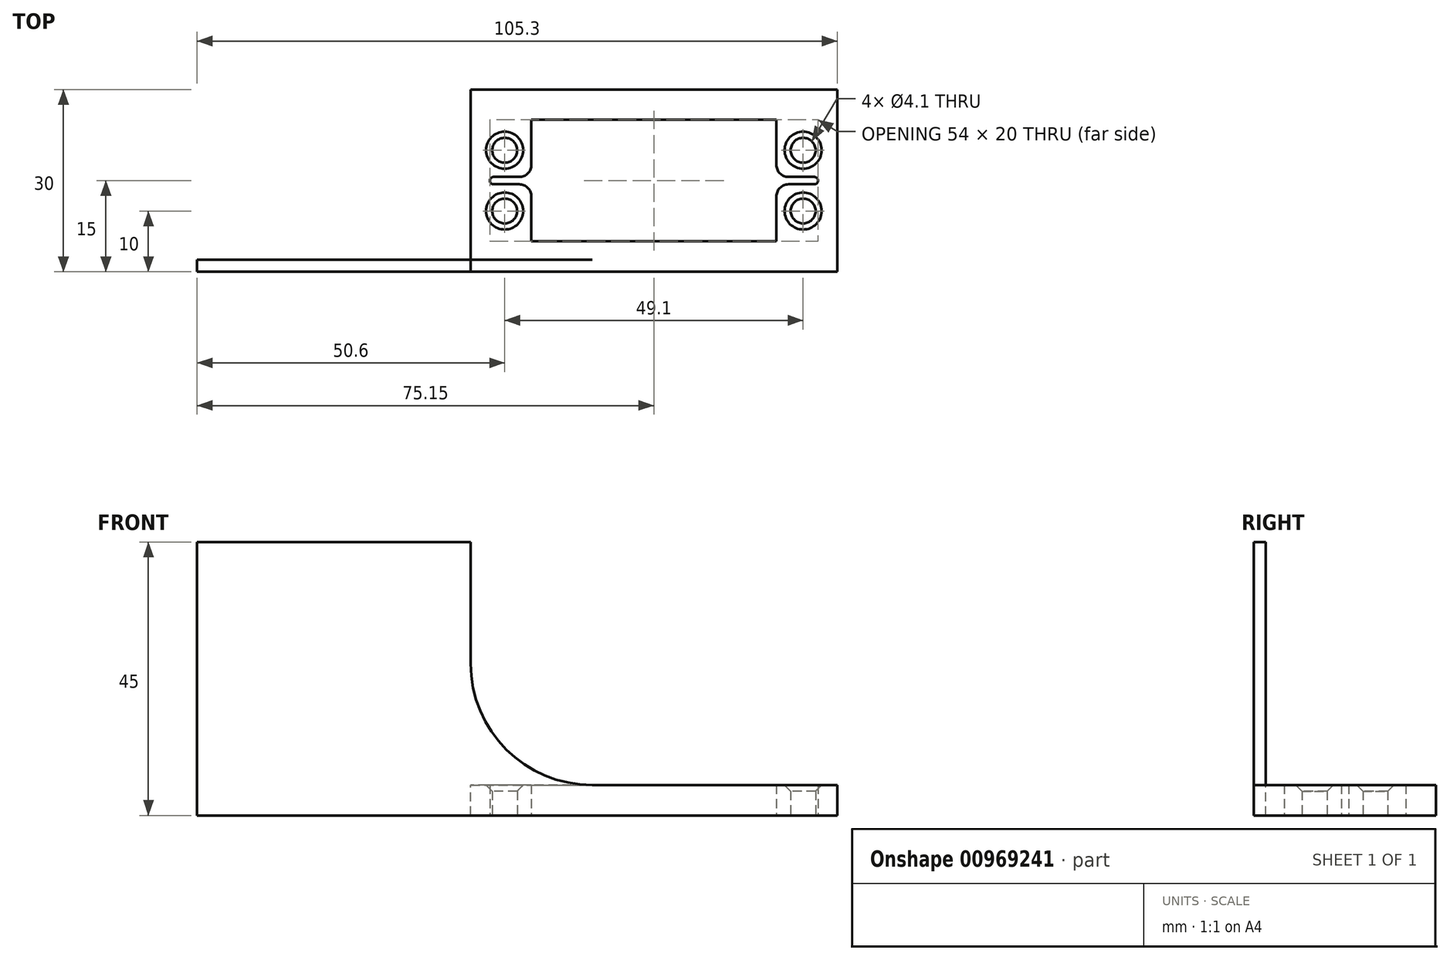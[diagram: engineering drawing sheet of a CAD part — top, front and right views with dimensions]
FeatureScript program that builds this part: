
annotation { "Feature Type Name" : "Feature", "Feature Type Description" : "" }
export const myFeature = defineFeature(function(context is Context, id is Id, definition is map)
    precondition{}
    {
        {
            var Q0;
            Q0=qCreatedBy(makeId("Top.planeOp"),FACE);
            var sketch = newSketch(context, id + "F0", { "sketchPlane" : qUnion([Q0])});
            skLineSegment(sketch, "E0.bottom", {"start": v(30.15, -15) * mm, "end": v(-30.15, -15) * mm});
            skLineSegment(sketch, "E0.top", {"start": v(30.15, 15) * mm, "end": v(-30.15, 15) * mm});
            skLineSegment(sketch, "E0.left", {"start": v(30.15, -15) * mm, "end": v(30.15, 15) * mm});
            skLineSegment(sketch, "E0.right", {"start": v(-30.15, -15) * mm, "end": v(-30.15, 15) * mm});
            skPoint(sketch, "E0.middle", {"position": v(0, 0) * mm});
            skLineSegment(sketch, "E1", {"start": v(0, 10) * mm, "end": v(20.15, 10) * mm});
            skLineSegment(sketch, "E2", {"start": v(20.15, 10) * mm, "end": v(20.15, 2.6) * mm});
            skLineSegment(sketch, "E3", {"start": v(22.15, 0.6) * mm, "end": v(26.4, 0.6) * mm});
            skLineSegment(sketch, "E4", {"start": v(27, 0) * mm, "end": v(27, 0) * mm});
            skPoint(sketch, "E5.visualSharp", {"position": v(27, 0.6) * mm});
            skArc(sketch, "E5.filletArc", {"start": v(27, 0) * mm, "mid": v(26.82, 0.42) * mm, "end": v(26.4, 0.6) * mm});
            skPoint(sketch, "E6.visualSharp", {"position": v(20.15, 0.6) * mm});
            skArc(sketch, "E6.filletArc", {"start": v(20.15, 2.6) * mm, "mid": v(20.74, 1.19) * mm, "end": v(22.15, 0.6) * mm});
            skLineSegment(sketch, "E7.MirrorCS", {"start": v(0, -10) * mm, "end": v(20.15, -10) * mm});
            skLineSegment(sketch, "E8.MirrorCS", {"start": v(20.15, -10) * mm, "end": v(20.15, -2.6) * mm});
            skArc(sketch, "E9.MirrorCS", {"start": v(20.15, -2.6) * mm, "mid": v(20.74, -1.19) * mm, "end": v(22.15, -0.6) * mm});
            skArc(sketch, "E10.MirrorCS", {"start": v(27, 0) * mm, "mid": v(26.82, -0.42) * mm, "end": v(26.4, -0.6) * mm});
            skLineSegment(sketch, "E11.MirrorCS", {"start": v(22.15, -0.6) * mm, "end": v(26.4, -0.6) * mm});
            skLineSegment(sketch, "E12.MirrorCS", {"start": v(0, 10) * mm, "end": v(-20.15, 10) * mm});
            skLineSegment(sketch, "E13.MirrorCS", {"start": v(-20.15, 10) * mm, "end": v(-20.15, 2.6) * mm});
            skArc(sketch, "E14.MirrorCS", {"start": v(-20.15, 2.6) * mm, "mid": v(-20.74, 1.19) * mm, "end": v(-22.15, 0.6) * mm});
            skLineSegment(sketch, "E15.MirrorCS", {"start": v(-22.15, 0.6) * mm, "end": v(-26.4, 0.6) * mm});
            skArc(sketch, "E16.MirrorCS", {"start": v(-27, 0) * mm, "mid": v(-26.82, -0.42) * mm, "end": v(-26.4, -0.6) * mm});
            skLineSegment(sketch, "E17.MirrorCS", {"start": v(-22.15, -0.6) * mm, "end": v(-26.4, -0.6) * mm});
            skArc(sketch, "E18.MirrorCS", {"start": v(-20.15, -2.6) * mm, "mid": v(-20.74, -1.19) * mm, "end": v(-22.15, -0.6) * mm});
            skLineSegment(sketch, "E19.MirrorCS", {"start": v(-20.15, -10) * mm, "end": v(-20.15, -2.6) * mm});
            skLineSegment(sketch, "E20.MirrorCS", {"start": v(0, -10) * mm, "end": v(-20.15, -10) * mm});
            skArc(sketch, "E21.MirrorCS", {"start": v(-27, 0) * mm, "mid": v(-26.82, 0.42) * mm, "end": v(-26.4, 0.6) * mm});
            skCircle(sketch, "E22", {"center": v(24.55, 5) * mm, "radius": 2.05 * mm});
            skCircle(sketch, "E23.MirrorC", {"center": v(-24.55, 5) * mm, "radius": 2.05 * mm});
            skCircle(sketch, "E24.MirrorC", {"center": v(-24.55, -5) * mm, "radius": 2.05 * mm});
            skCircle(sketch, "E25.MirrorC", {"center": v(24.55, -5) * mm, "radius": 2.05 * mm});
            skSolve(sketch);
        }
        {
            var Q0;
            Q0 = qSketchRegion(id + "F0", true);
            extrude(context, id + "F1", {"entities" : qUnion([Q0]), "depth" : 5 * mm, "offsetDistance" : 25 * mm});
        }
        {
            var Q0;
            Q0=makeQuery(id+"F1.opExtrude","SWEPT_FACE",FACE,{"disambiguationData":[OSD([sQuery(id+"F0.wireOp",EDGE,"E0.bottom")])]});
            var sketch = newSketch(context, id + "F2", { "sketchPlane" : qUnion([Q0])});
            skLineSegment(sketch, "E26", {"start": v(-10.03, 0) * mm, "end": v(-75.15, 0) * mm});
            skLineSegment(sketch, "E27", {"start": v(-75.15, 0) * mm, "end": v(-75.15, 45) * mm});
            skLineSegment(sketch, "E28", {"start": v(-75.15, 45) * mm, "end": v(-30.15, 45) * mm});
            skLineSegment(sketch, "E29", {"start": v(-30.15, 45) * mm, "end": v(-30.15, 25) * mm});
            skLineSegment(sketch, "E30", {"start": v(-10.03, 0) * mm, "end": v(-10.03, 5) * mm});
            skLineSegment(sketch, "E31", {"start": v(-10.03, 5) * mm, "end": v(-10.15, 5) * mm});
            skPoint(sketch, "E32.visualSharp", {"position": v(-30.15, 5) * mm});
            skArc(sketch, "E32.filletArc", {"start": v(-30.15, 25) * mm, "mid": v(-24.3, 10.86) * mm, "end": v(-10.15, 5) * mm});
            skSolve(sketch);
        }
        {
            var Q0;
            Q0 = qSketchRegion(id + "F2", true);
            extrude(context, id + "F3", {"entities" : qUnion([Q0]), "operationType" : NewBodyOperationType.ADD, "oppositeDirection" : true, "depth" : 2 * mm, "offsetDistance" : 25 * mm});
        }
        {
            var Q0;
            Q0=makeQuery(id+"F1.opExtrude","CAP_EDGE",EDGE,{"disambiguationData":[OSD([sQuery(id+"F0.wireOp",EDGE,"E24.MirrorC")])],"isStart":false});
            var Q1;
            Q1=makeQuery(id+"F1.opExtrude","CAP_EDGE",EDGE,{"disambiguationData":[OSD([sQuery(id+"F0.wireOp",EDGE,"E23.MirrorC")])],"isStart":false});
            var Q2;
            Q2=makeQuery(id+"F1.opExtrude","CAP_EDGE",EDGE,{"disambiguationData":[OSD([sQuery(id+"F0.wireOp",EDGE,"E25.MirrorC")])],"isStart":false});
            var Q3;
            Q3=makeQuery(id+"F1.opExtrude","CAP_EDGE",EDGE,{"disambiguationData":[OSD([sQuery(id+"F0.wireOp",EDGE,"E22")])],"isStart":false});
            chamfer(context, id + "F4", {"entities" : qUnion([Q0, Q1, Q2, Q3]), "width" : 1 * mm, "tangentPropagation" : true});
        }
    });
